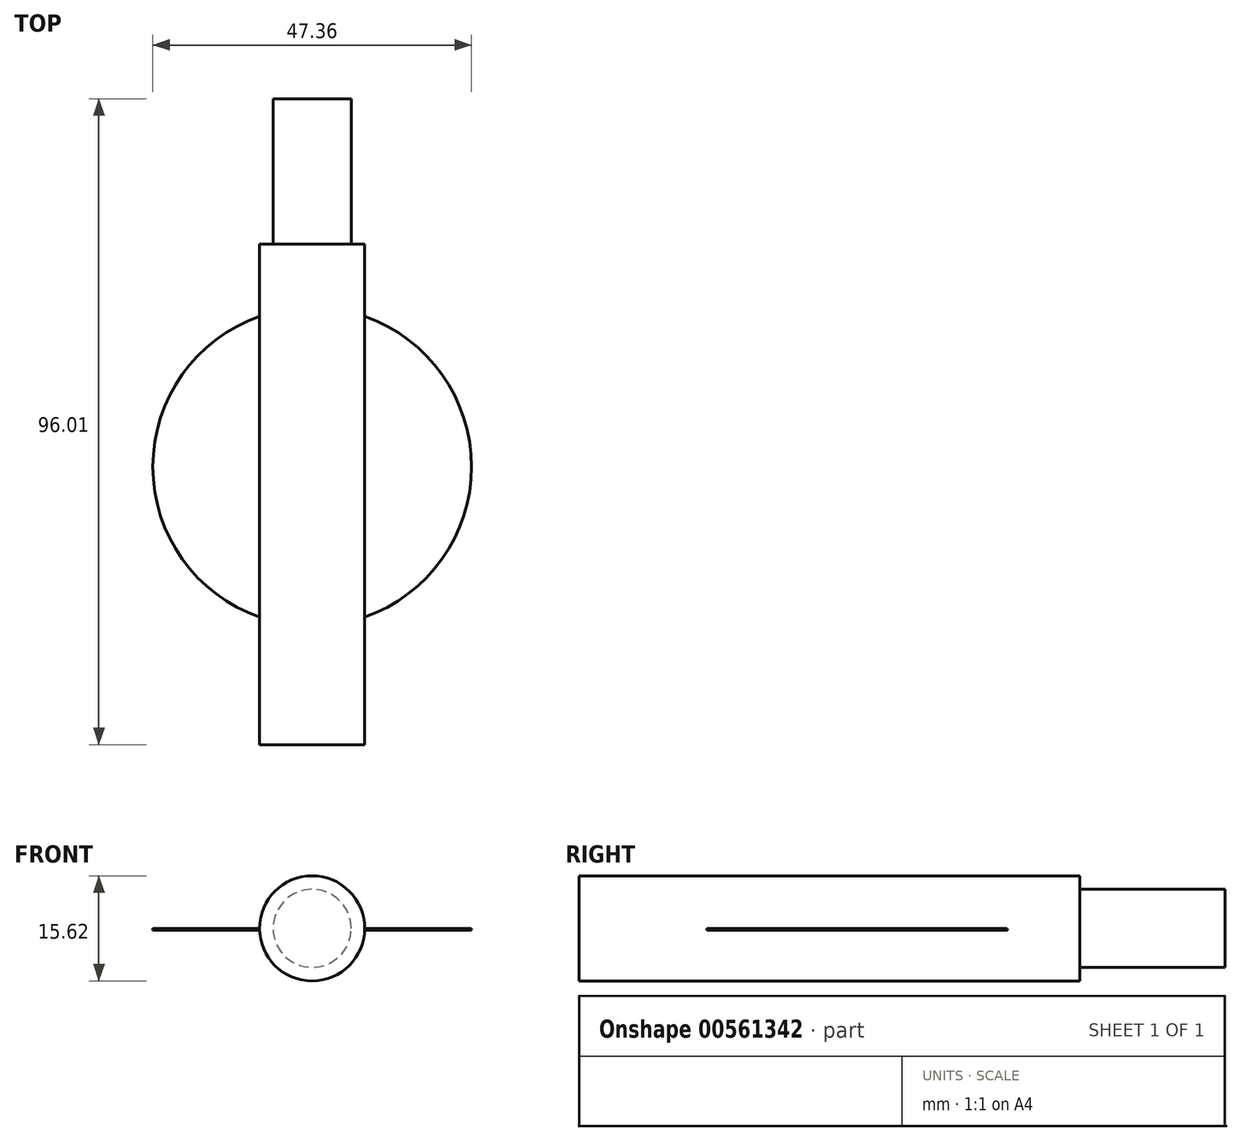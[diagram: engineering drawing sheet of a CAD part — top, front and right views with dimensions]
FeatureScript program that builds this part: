
annotation { "Feature Type Name" : "Feature", "Feature Type Description" : "" }
export const myFeature = defineFeature(function(context is Context, id is Id, definition is map)
    precondition{}
    {
        {
            var Q0;
            Q0=qCreatedBy(makeId("Front.planeOp"),FACE);
            var sketch = newSketch(context, id + "F0", { "sketchPlane" : qUnion([Q0])});
            skCircle(sketch, "E0", {"center": v(0, 0) * mm, "radius": 7.81 * mm});
            skSolve(sketch);
        }
        {
            var Q0;
            Q0=makeQuery(id+"F0.imprint","IMPRINT",FACE,{"disambiguationData":[TD([[makeQuery(id+"F0.imprint","IMPRINT",EDGE,{"derivedFrom":sQuery(id+"F0.wireOp",EDGE,"E0")}),1.0]])]});
            extrude(context, id + "F1", {"entities" : qUnion([Q0]), "depth" : 74.42 * mm, "offsetDistance" : 25.4 * mm});
        }
        {
            var Q0;
            Q0=qCreatedBy(makeId("Front.planeOp"),FACE);
            var sketch = newSketch(context, id + "F2", { "sketchPlane" : qUnion([Q0])});
            skCircle(sketch, "E1", {"center": v(0, 0) * mm, "radius": 5.8 * mm});
            skSolve(sketch);
        }
        {
            var Q0;
            Q0 = qSketchRegion(id + "F2", true);
            extrude(context, id + "F3", {"entities" : qUnion([Q0]), "operationType" : NewBodyOperationType.ADD, "oppositeDirection" : true, "depth" : 21.59 * mm, "offsetDistance" : 25.4 * mm});
        }
        {
            var Q0;
            Q0=qCreatedBy(makeId("Top.planeOp"),FACE);
            var sketch = newSketch(context, id + "F4", { "sketchPlane" : qUnion([Q0])});
            skCircle(sketch, "E2", {"center": v(0, -33.12) * mm, "radius": 23.68 * mm});
            skSolve(sketch);
        }
        {
            var Q0;
            Q0 = qSketchRegion(id + "F4", true);
            extrude(context, id + "F5", {"entities" : qUnion([Q0]), "operationType" : NewBodyOperationType.ADD, "oppositeDirection" : true, "depth" : 0.25 * mm, "offsetDistance" : 25.4 * mm});
        }
    });
